# Revit family: 95801024
name_source: partatom
category: Equipamento especial
revit_build: Autodesk Revit 2016 (Build: 20150220_1215(x64)
units: mm (PartAtom-declared; Revit-internal decimal feet)

## family parameters
Com base no plano de trabalho = Não
Compartilhado = Não
Corte com vazios quando carregados = Não
Cota do conector redondo = Utilizar diâmetro
Ponto de cálculo do ambiente = Não
Sempre na vertical = Sim
Tipo de parte = Normal

## types (1)
- Tramontina Dritta Split 90 Iha - 95801024
    Classe de Construção = Classe I
    Código de montagem = 95801024
    Descrição = 95801024
    Desenvolvedor = Factory Cursos & Desenvolvimento
    Disjuntor termomagnético = 10 A
    Fabricante = Tramontina
    Frequência = 60 Hz
    Grau de proteção = IPX0
    Iluminação (2 x 1,0 W - 12 V ) = Lampadas Led - Cor 3200 K
    Modelo = Tramontina Dritta Split 90 Iha - 945800024
    Nivel de Ruido = 63 dB
    Numero de Velocidades = 3
    Potência Elétrica = 190 W
    Potência Motor = 185 W
    Referencia Tramontina = 95801024
    Site do desenvolvedor = www.factorycursos.com.br
    Tensão = 220 V
    URL = https://tramontina.com

## geometry (parser evidence)
native form markers: Blend x2
no freeform markers — native parametric forms only
